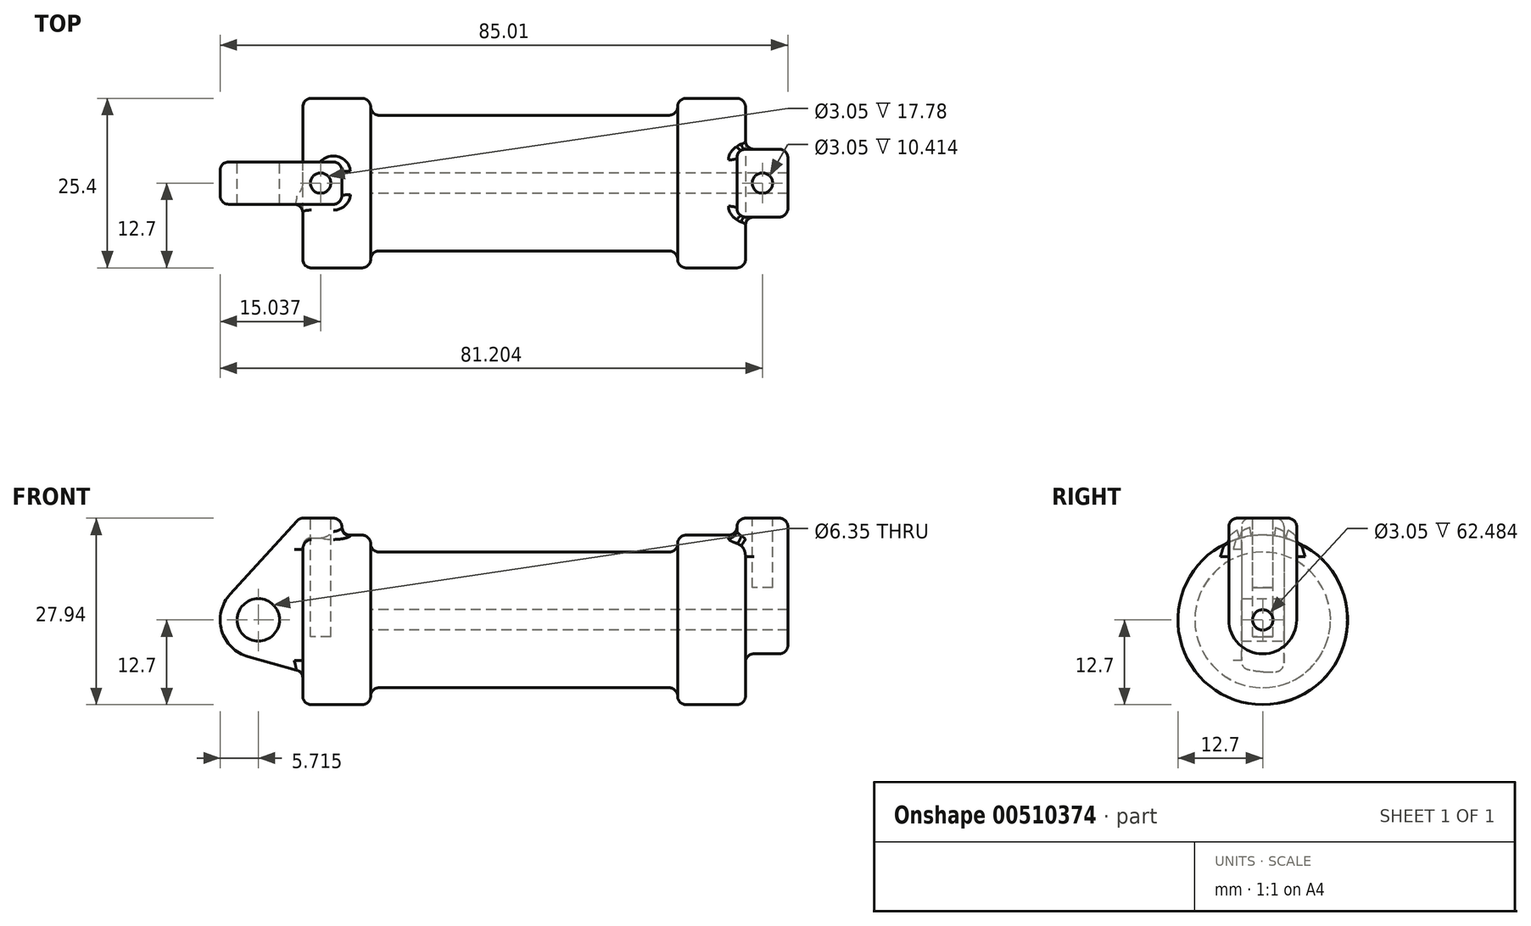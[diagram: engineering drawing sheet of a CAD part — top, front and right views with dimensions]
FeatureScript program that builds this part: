
annotation { "Feature Type Name" : "Feature", "Feature Type Description" : "" }
export const myFeature = defineFeature(function(context is Context, id is Id, definition is map)
    precondition{}
    {
        {
            var Q0;
            Q0=qCreatedBy(makeId("Front.planeOp"),FACE);
            var sketch = newSketch(context, id + "F0", { "sketchPlane" : qUnion([Q0])});
            skLineSegment(sketch, "E0", {"start": v(0, 0) * mm, "end": v(0, 12.7) * mm});
            skLineSegment(sketch, "E1", {"start": v(0, 12.7) * mm, "end": v(10.16, 12.7) * mm});
            skLineSegment(sketch, "E2", {"start": v(10.16, 12.7) * mm, "end": v(10.16, 10.16) * mm});
            skLineSegment(sketch, "E3", {"start": v(10.16, 10.16) * mm, "end": v(56.13, 10.16) * mm});
            skLineSegment(sketch, "E4", {"start": v(56.13, 10.16) * mm, "end": v(56.13, 12.7) * mm});
            skLineSegment(sketch, "E5", {"start": v(56.13, 12.7) * mm, "end": v(66.3, 12.7) * mm});
            skLineSegment(sketch, "E6", {"start": v(66.3, 12.7) * mm, "end": v(66.3, 0) * mm});
            skLineSegment(sketch, "E7", {"start": v(66.3, 0) * mm, "end": v(0, 0) * mm});
            skLineSegment(sketch, "E8", {"start": v(5.84, 15.24) * mm, "end": v(-0.5, 15.24) * mm});
            skLineSegment(sketch, "E9", {"start": v(-0.5, 15.24) * mm, "end": v(-10.88, 3.85) * mm});
            skLineSegment(sketch, "E10", {"start": v(0, 0) * mm, "end": v(-6.65, 0) * mm});
            skCircle(sketch, "E11", {"center": v(-6.65, 0) * mm, "radius": 5.72 * mm});
            skCircle(sketch, "E12", {"center": v(-6.65, 0) * mm, "radius": 3.18 * mm});
            skLineSegment(sketch, "E13", {"start": v(5.84, 15.24) * mm, "end": v(5.84, -9.4) * mm});
            skLineSegment(sketch, "E14", {"start": v(5.84, -9.4) * mm, "end": v(-8.18, -5.5) * mm});
            skSolve(sketch);
        }
        {
            var Q0;
            {var subQ0=sQuery(id+"F0.wireOp",EDGE,"E2");Q0=makeQuery(id+"F0.imprint","IMPRINT",FACE,{"disambiguationData":[TD([[makeQuery(id+"F0.imprint","IMPRINT",EDGE,{"derivedFrom":subQ0}),-1.0]])]});}
            var Q1;
            {var subQ0=sQuery(id+"F0.wireOp",EDGE,"E0");Q1=makeQuery(id+"F0.imprint","IMPRINT",FACE,{"disambiguationData":[TD([[makeQuery(id+"F0.imprint","IMPRINT",EDGE,{"derivedFrom":subQ0}),-1.0]])]});}
            var Q2;
            Q2=sQuery(id+"F0.wireOp",EDGE,"E7");
            revolve(context, id + "F1", {"entities" : qUnion([Q0, Q1]), "axis" : qUnion([Q2]), "revolveType" : RevolveType.FULL});
        }
        {
            var Q0;
            {var subQ4=sQuery(id+"F0.wireOp",EDGE,"E12");Q0=makeQuery(id+"F0.imprint","IMPRINT",FACE,{"disambiguationData":[TD([[makeQuery(id+"F0.imprint","IMPRINT",EDGE,{"derivedFrom":subQ4}),-1.0]])]});}
            var Q1;
            {var subQ3=sQuery(id+"F0.wireOp",EDGE,"E0");Q1=makeQuery(id+"F0.imprint","IMPRINT",FACE,{"disambiguationData":[TD([[makeQuery(id+"F0.imprint","IMPRINT",EDGE,{"derivedFrom":subQ3}),1.0]])]});}
            var Q2;
            {var subQ0=sQuery(id+"F0.wireOp",EDGE,"E14");Q2=makeQuery(id+"F0.imprint","IMPRINT",FACE,{"disambiguationData":[TD([[makeQuery(id+"F0.imprint","IMPRINT",EDGE,{"derivedFrom":subQ0}),-1.0]])]});}
            var Q3;
            {var subQ0=sQuery(id+"F0.wireOp",EDGE,"E0");Q3=makeQuery(id+"F0.imprint","IMPRINT",FACE,{"disambiguationData":[TD([[makeQuery(id+"F0.imprint","IMPRINT",EDGE,{"derivedFrom":subQ0}),-1.0]])]});}
            extrude(context, id + "F2", {"entities" : qUnion([Q0, Q1, Q2, Q3]), "operationType" : NewBodyOperationType.ADD, "endBound" : BoundingType.SYMMETRIC, "depth" : 6.35 * mm});
        }
        {
            var Q0;
            Q0=makeQuery(id+"F1.opRevolve","SWEPT_FACE",FACE,{"disambiguationData":[OSD([sQuery(id+"F0.wireOp",EDGE,"E6")])]});
            var sketch = newSketch(context, id + "F3", { "sketchPlane" : qUnion([Q0])});
            skCircle(sketch, "E15", {"center": v(0, 0) * mm, "radius": 1.52 * mm});
            skCircle(sketch, "E16", {"center": v(0, 0) * mm, "radius": 5.08 * mm});
            skLineSegment(sketch, "E17", {"start": v(5.08, 0) * mm, "end": v(5.08, 15.24) * mm});
            skLineSegment(sketch, "E18", {"start": v(-5.08, 0) * mm, "end": v(-5.08, 15.24) * mm});
            skLineSegment(sketch, "E19", {"start": v(-5.08, 15.24) * mm, "end": v(5.08, 15.24) * mm});
            skSolve(sketch);
        }
        {
            var Q0;
            Q0=qSketchRegion(id+"F3",true);
            extrude(context, id + "F4", {"entities" : qUnion([Q0]), "operationType" : NewBodyOperationType.ADD, "depth" : 6.35 * mm, "hasSecondDirection" : true, "secondDirectionOppositeDirection" : true, "secondDirectionDepth" : 1.27 * mm});
        }
        {
            var Q0;
            Q0=makeQuery(id+"F3.imprint","IMPRINT",FACE,{"disambiguationData":[TD([[makeQuery(id+"F3.imprint","IMPRINT",EDGE,{"derivedFrom":sQuery(id+"F3.wireOp",EDGE,"E15")}),1.0]])]});
            var Q1;
            Q1=makeQuery(id+"F1.opRevolve","SWEPT_FACE",FACE,{"disambiguationData":[OSD([sQuery(id+"F0.wireOp",EDGE,"E2")])]});
            extrude(context, id + "F5", {"entities" : qUnion([Q0]), "operationType" : NewBodyOperationType.REMOVE, "endBound" : BoundingType.UP_TO_SURFACE, "oppositeDirection" : true, "endBoundEntityFace" : qUnion([Q1]), "depth" : 25.4 * mm});
        }
        {
            var Q0;
            Q0=makeQuery(id+"F4.opExtrude","SWEPT_FACE",FACE,{"disambiguationData":[OSD([sQuery(id+"F3.wireOp",EDGE,"E19")])]});
            var sketch = newSketch(context, id + "F6", { "sketchPlane" : qUnion([Q0])});
            skLineSegment(sketch, "E20.0", {"start": v(5.84, 3.18) * mm, "end": v(-0.5, 3.18) * mm, "construction": true});
            skLineSegment(sketch, "E21.0", {"start": v(-0.5, -3.18) * mm, "end": v(-0.5, 3.17) * mm, "construction": true});
            skLineSegment(sketch, "E22.0", {"start": v(72.64, 5.08) * mm, "end": v(65.02, 5.08) * mm, "construction": true});
            skLineSegment(sketch, "E23.0", {"start": v(72.64, -5.08) * mm, "end": v(72.64, 5.08) * mm, "construction": true});
            skCircle(sketch, "E24", {"center": v(2.67, 0) * mm, "radius": 1.52 * mm});
            skPoint(sketch, "E24.centerSnap0", {"position": v(2.67, 3.18) * mm});
            skPoint(sketch, "E24.centerSnap1", {"position": v(-0.5, 0) * mm});
            skCircle(sketch, "E25", {"center": v(68.83, 0) * mm, "radius": 1.52 * mm});
            skPoint(sketch, "E25.centerSnap0", {"position": v(72.64, 0) * mm});
            skPoint(sketch, "E25.centerSnap1", {"position": v(68.83, 5.08) * mm});
            skSolve(sketch);
        }
        {
            var Q0;
            Q0=makeQuery(id+"F6.imprint","IMPRINT",FACE,{"disambiguationData":[TD([[makeQuery(id+"F6.imprint","IMPRINT",EDGE,{"derivedFrom":sQuery(id+"F6.wireOp",EDGE,"E24")}),1.0]])]});
            extrude(context, id + "F7", {"entities" : qUnion([Q0]), "operationType" : NewBodyOperationType.REMOVE, "oppositeDirection" : true, "depth" : 17.78 * mm});
        }
        {
            var Q0;
            Q0=makeQuery(id+"F6.imprint","IMPRINT",FACE,{"disambiguationData":[TD([[makeQuery(id+"F6.imprint","IMPRINT",EDGE,{"derivedFrom":sQuery(id+"F6.wireOp",EDGE,"E25")}),1.0]])]});
            extrude(context, id + "F8", {"entities" : qUnion([Q0]), "operationType" : NewBodyOperationType.REMOVE, "oppositeDirection" : true, "depth" : 10.4 * mm});
        }
        {
            var Q0;
            Q0=makeQuery(id+"F1.opRevolve","SWEPT_EDGE",EDGE,{"disambiguationData":[OSD([sQuery(id+"F0.wireOp",EDGE,"E0"),sQuery(id+"F0.wireOp",EDGE,"E1")])]});
            var Q1;
            Q1=makeQuery(id+"F1.opRevolve","SWEPT_EDGE",EDGE,{"disambiguationData":[OSD([sQuery(id+"F0.wireOp",EDGE,"E1"),sQuery(id+"F0.wireOp",EDGE,"E2")])]});
            var Q2;
            Q2=makeQuery(id+"F1.opRevolve","SWEPT_EDGE",EDGE,{"disambiguationData":[OSD([sQuery(id+"F0.wireOp",EDGE,"E2"),sQuery(id+"F0.wireOp",EDGE,"E3")])]});
            var Q3;
            Q3=makeQuery(id+"F1.opRevolve","SWEPT_EDGE",EDGE,{"disambiguationData":[OSD([sQuery(id+"F0.wireOp",EDGE,"E4"),sQuery(id+"F0.wireOp",EDGE,"E5")])]});
            var Q4;
            Q4=makeQuery(id+"F1.opRevolve","SWEPT_EDGE",EDGE,{"disambiguationData":[OSD([sQuery(id+"F0.wireOp",EDGE,"E5"),sQuery(id+"F0.wireOp",EDGE,"E6")])]});
            var Q5;
            Q5=makeQuery(id+"F1.opRevolve","SWEPT_EDGE",EDGE,{"disambiguationData":[OSD([sQuery(id+"F0.wireOp",EDGE,"E3"),sQuery(id+"F0.wireOp",EDGE,"E4")])]});
            fillet(context, id + "F9", {"entities" : qUnion([Q0, Q1, Q2, Q3, Q4, Q5]), "radius" : 1.27 * mm, "tangentPropagation" : true, "allowEdgeOverflow" : false});
        }
        {
            var Q0;
            Q0=makeQuery(id+"F2.opExtrude","CAP_EDGE",EDGE,{"disambiguationData":[OSD([sQuery(id+"F0.wireOp",EDGE,"E14")])],"isStart":false});
            var Q1;
            Q1=makeQuery(id+"F2.opExtrude","SWEPT_EDGE",EDGE,{"disambiguationData":[OSD([sQuery(id+"F0.wireOp",EDGE,"E8"),sQuery(id+"F0.wireOp",EDGE,"E9")])]});
            var Q2;
            Q2=makeQuery(id+"F2.opExtrude","CAP_EDGE",EDGE,{"disambiguationData":[OSD([sQuery(id+"F0.wireOp",EDGE,"E8")])],"isStart":false});
            var Q3;
            Q3=makeQuery(id+"F2.opExtrude","CAP_EDGE",EDGE,{"disambiguationData":[OSD([sQuery(id+"F0.wireOp",EDGE,"E8")])],"isStart":true});
            var Q4;
            Q4=makeQuery(id+"F2.opExtrude","CAP_EDGE",EDGE,{"disambiguationData":[OSD([sQuery(id+"F0.wireOp",EDGE,"E9")])],"isStart":true});
            var Q5;
            Q5=makeQuery(id+"F2.boolean.opBoolean","INTERSECT",EDGE,{"derivedFrom":[makeQuery(id+"F1.opRevolve","SWEPT_FACE",FACE,{"disambiguationData":[OSD([sQuery(id+"F0.wireOp",EDGE,"E0")])]}),makeQuery(id+"F2.opExtrude","CAP_FACE",FACE,{"disambiguationData":[OSD([sQuery(id+"F0.wireOp",EDGE,"E8"),sQuery(id+"F0.wireOp",EDGE,"E9"),sQuery(id+"F0.wireOp",EDGE,"E11"),sQuery(id+"F0.wireOp",EDGE,"E12"),sQuery(id+"F0.wireOp",EDGE,"E13"),sQuery(id+"F0.wireOp",EDGE,"E14")])],"isStart":false})]});
            var Q6;
            Q6=makeQuery(id+"F2.boolean.opBoolean","INTERSECT",EDGE,{"derivedFrom":[makeQuery(id+"F1.opRevolve","SWEPT_FACE",FACE,{"disambiguationData":[OSD([sQuery(id+"F0.wireOp",EDGE,"E1")])]}),makeQuery(id+"F2.opExtrude","SWEPT_FACE",FACE,{"disambiguationData":[OSD([sQuery(id+"F0.wireOp",EDGE,"E13")])]})]});
            var Q7;
            Q7=makeQuery(id+"F2.opExtrude","CAP_EDGE",EDGE,{"disambiguationData":[OSD([sQuery(id+"F0.wireOp",EDGE,"E13")])],"isStart":false});
            var Q8;
            Q8=makeQuery(id+"F2.opExtrude","CAP_EDGE",EDGE,{"disambiguationData":[OSD([sQuery(id+"F0.wireOp",EDGE,"E13")])],"isStart":true});
            var Q9;
            Q9=makeQuery(id+"F2.opExtrude","SWEPT_EDGE",EDGE,{"disambiguationData":[OSD([sQuery(id+"F0.wireOp",EDGE,"E8"),sQuery(id+"F0.wireOp",EDGE,"E13")])]});
            fillet(context, id + "F10", {"entities" : qUnion([Q0, Q1, Q2, Q3, Q4, Q5, Q6, Q7, Q8, Q9]), "radius" : 1.27 * mm, "tangentPropagation" : true, "allowEdgeOverflow" : false});
        }
        {
            var Q0;
            Q0=makeQuery(id+"F4.opExtrude","CAP_FACE",FACE,{"disambiguationData":[OSD([sQuery(id+"F3.wireOp",EDGE,"E15"),sQuery(id+"F3.wireOp",EDGE,"E16"),sQuery(id+"F3.wireOp",EDGE,"E17"),sQuery(id+"F3.wireOp",EDGE,"E18"),sQuery(id+"F3.wireOp",EDGE,"E19")])],"isStart":true});
            var Q1;
            Q1=makeQuery(id+"F4.opExtrude","SWEPT_FACE",FACE,{"disambiguationData":[OSD([sQuery(id+"F3.wireOp",EDGE,"E18")])]});
            var Q2;
            Q2=makeQuery(id+"F4.opExtrude","CAP_EDGE",EDGE,{"disambiguationData":[OSD([sQuery(id+"F3.wireOp",EDGE,"E19")])],"isStart":false});
            var Q3;
            Q3=makeQuery(id+"F4.opExtrude","SWEPT_EDGE",EDGE,{"disambiguationData":[OSD([sQuery(id+"F3.wireOp",EDGE,"E17"),sQuery(id+"F3.wireOp",EDGE,"E19")])]});
            fillet(context, id + "F11", {"entities" : qUnion([Q0, Q1, Q2, Q3]), "radius" : 1.27 * mm, "tangentPropagation" : true, "allowEdgeOverflow" : false});
        }
    });
